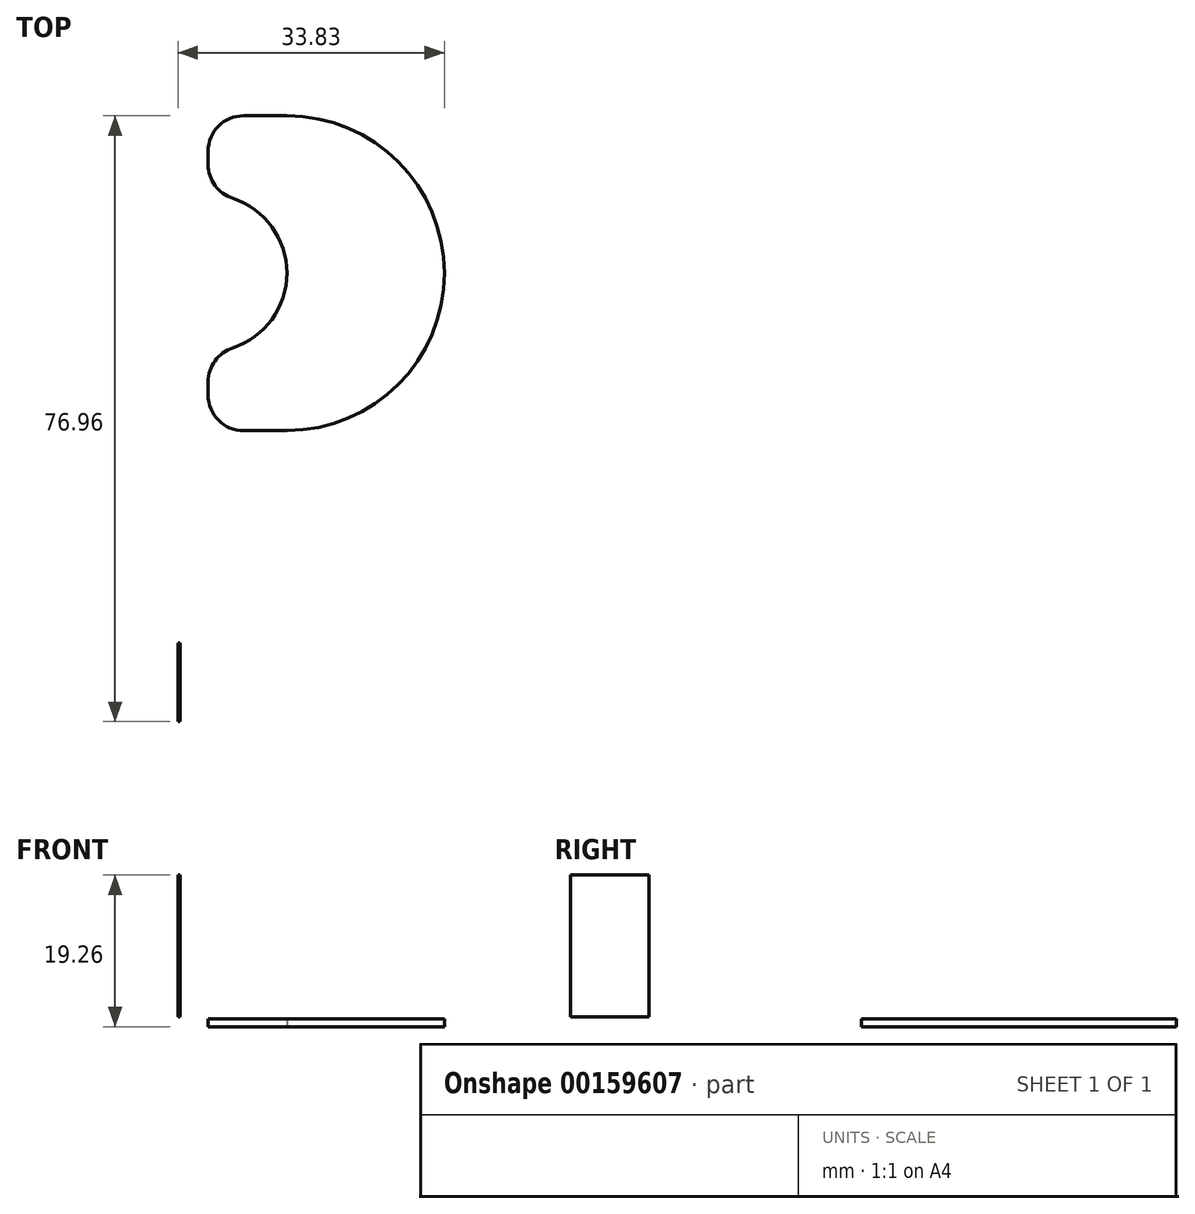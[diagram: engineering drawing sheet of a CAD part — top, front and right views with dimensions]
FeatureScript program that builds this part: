
annotation { "Feature Type Name" : "Feature", "Feature Type Description" : "" }
export const myFeature = defineFeature(function(context is Context, id is Id, definition is map)
    precondition{}
    {
        {
            assignVariable(context, id + "F0", {"name" : "W", "anyValue" : 1});
        }
        {
            var Q0;
            Q0=qCreatedBy(makeId("Top.planeOp"),FACE);
            var sketch = newSketch(context, id + "F1", { "sketchPlane" : qUnion([Q0])});
            skArc(sketch, "E0", {"start": v(3.83, 8.46) * mm, "mid": v(13.83, 18.46) * mm, "end": v(3.83, 28.46) * mm});
            skArc(sketch, "E1", {"start": v(13.83, -1.54) * mm, "mid": v(33.83, 18.46) * mm, "end": v(13.83, 38.46) * mm});
            skLineSegment(sketch, "E2", {"start": v(3.83, 8.46) * mm, "end": v(3.83, -1.54) * mm});
            skLineSegment(sketch, "E3", {"start": v(3.83, -1.54) * mm, "end": v(13.83, -1.54) * mm});
            skLineSegment(sketch, "E4", {"start": v(13.83, 38.46) * mm, "end": v(3.83, 38.46) * mm});
            skLineSegment(sketch, "E5", {"start": v(3.83, 38.46) * mm, "end": v(3.83, 28.46) * mm});
            skSolve(sketch);
        }
        {
            var Q0;
            Q0=qCreatedBy(makeId("Right.planeOp"),FACE);
            var sketch = newSketch(context, id + "F2", { "sketchPlane" : qUnion([Q0])});
            skLineSegment(sketch, "E6.bottom", {"start": v(-38.5, 19.26) * mm, "end": v(-28.5, 19.26) * mm});
            skLineSegment(sketch, "E6.top", {"start": v(-38.5, 1.26) * mm, "end": v(-28.5, 1.26) * mm});
            skLineSegment(sketch, "E6.left", {"start": v(-38.5, 19.26) * mm, "end": v(-38.5, 1.26) * mm});
            skLineSegment(sketch, "E6.right", {"start": v(-28.5, 19.26) * mm, "end": v(-28.5, 1.26) * mm});
            skSolve(sketch);
        }
        {
            var Q0;
            Q0 = qSketchRegion(id + "F2", true);
            extrude(context, id + "F3", {"entities" : qUnion([Q0]), "depth" : (getVariable(context, 'W') * 1 / 4) * mm});
        }
        {
            var Q0;
            Q0=makeQuery(id+"F1.imprint","IMPRINT",FACE,{"disambiguationData":[TD([[makeQuery(id+"F1.imprint","IMPRINT",EDGE,{"derivedFrom":sQuery(id+"F1.wireOp",EDGE,"E0")}),-1.0]])]});
            extrude(context, id + "F4", {"entities" : qUnion([Q0]), "depth" : (getVariable(context, 'W')) * mm});
        }
        {
            var Q0;
            Q0=makeQuery(id+"F4.opExtrude","SWEPT_EDGE",EDGE,{"disambiguationData":[OSD([sQuery(id+"F1.wireOp",EDGE,"E0"),sQuery(id+"F1.wireOp",EDGE,"E5")])]});
            fillet(context, id + "F5", {"entities" : qUnion([Q0]), "radius" : 4.5 * mm, "tangentPropagation" : true, "allowEdgeOverflow" : false});
        }
        {
            var Q0;
            Q0=makeQuery(id+"F4.opExtrude","SWEPT_EDGE",EDGE,{"disambiguationData":[OSD([sQuery(id+"F1.wireOp",EDGE,"E4"),sQuery(id+"F1.wireOp",EDGE,"E5")])]});
            fillet(context, id + "F6", {"entities" : qUnion([Q0]), "radius" : 4.5 * mm, "tangentPropagation" : true, "allowEdgeOverflow" : false});
        }
        {
            var Q0;
            Q0=makeQuery(id+"F4.opExtrude","SWEPT_EDGE",EDGE,{"disambiguationData":[OSD([sQuery(id+"F1.wireOp",EDGE,"E0"),sQuery(id+"F1.wireOp",EDGE,"E2")])]});
            fillet(context, id + "F7", {"entities" : qUnion([Q0]), "radius" : 4.5 * mm, "tangentPropagation" : true, "allowEdgeOverflow" : false});
        }
        {
            var Q0;
            Q0=makeQuery(id+"F4.opExtrude","SWEPT_EDGE",EDGE,{"disambiguationData":[OSD([sQuery(id+"F1.wireOp",EDGE,"E2"),sQuery(id+"F1.wireOp",EDGE,"E3")])]});
            fillet(context, id + "F8", {"entities" : qUnion([Q0]), "radius" : 4.5 * mm, "tangentPropagation" : true, "allowEdgeOverflow" : false});
        }
    });
